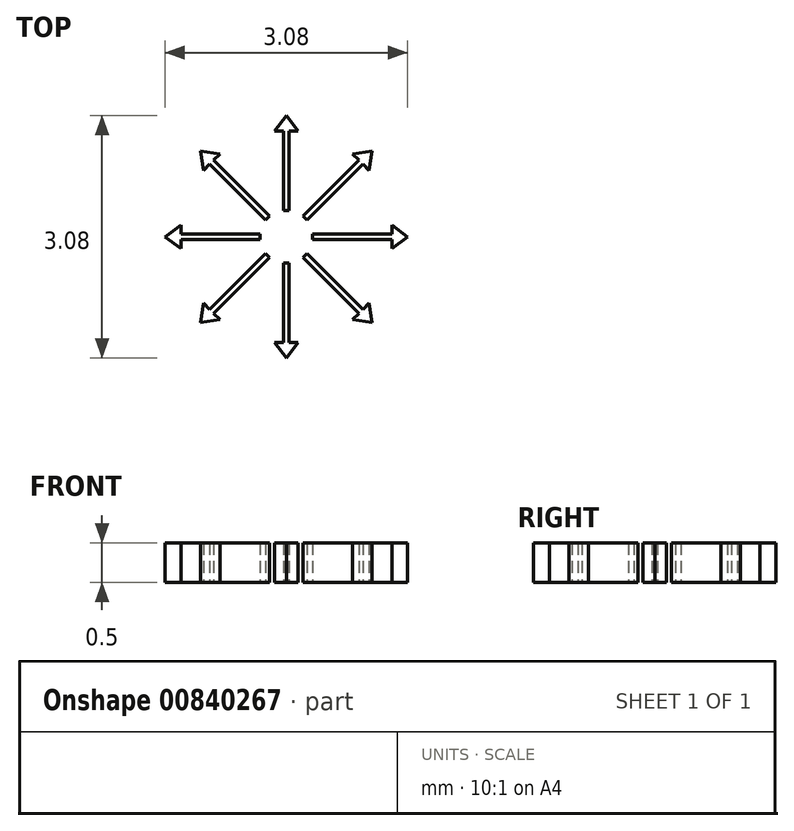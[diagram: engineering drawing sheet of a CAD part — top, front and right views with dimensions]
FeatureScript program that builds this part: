
annotation { "Feature Type Name" : "Feature", "Feature Type Description" : "" }
export const myFeature = defineFeature(function(context is Context, id is Id, definition is map)
    precondition{}
    {
        {
            var Q0;
            Q0=qCreatedBy(makeId("Top.planeOp"),FACE);
            var sketch = newSketch(context, id + "F0", { "sketchPlane" : qUnion([Q0])});
            skPoint(sketch, "E0.center", {"position": v(0, 0) * mm});
            skLineSegment(sketch, "E1", {"start": v(-0.04, 1.34) * mm, "end": v(-0.04, 0.34) * mm});
            skLineSegment(sketch, "E2", {"start": v(0.04, 1.34) * mm, "end": v(0.04, 0.34) * mm});
            skLineSegment(sketch, "E3", {"start": v(-0.04, 0.34) * mm, "end": v(0.04, 0.34) * mm});
            skLineSegment(sketch, "E4", {"start": v(-0.04, 1.34) * mm, "end": v(0.04, 1.34) * mm});
            skLineSegment(sketch, "E5", {"start": v(-0.04, 1.34) * mm, "end": v(-0.15, 1.34) * mm});
            skLineSegment(sketch, "E6", {"start": v(-0.15, 1.34) * mm, "end": v(0, 1.54) * mm});
            skLineSegment(sketch, "E7", {"start": v(0.04, 1.34) * mm, "end": v(0.15, 1.34) * mm});
            skLineSegment(sketch, "E8", {"start": v(0.15, 1.34) * mm, "end": v(0, 1.54) * mm});
            skLineSegment(sketch, "E9.1.0", {"start": v(-0.92, 0.97) * mm, "end": v(-0.21, 0.26) * mm});
            skLineSegment(sketch, "E9.1.1", {"start": v(-1.05, 0.84) * mm, "end": v(-1.09, 1.09) * mm});
            skLineSegment(sketch, "E9.1.2", {"start": v(-0.97, 0.92) * mm, "end": v(-0.26, 0.21) * mm});
            skLineSegment(sketch, "E9.1.4", {"start": v(-0.84, 1.05) * mm, "end": v(-1.09, 1.09) * mm});
            skLineSegment(sketch, "E9.1.5", {"start": v(-0.97, 0.92) * mm, "end": v(-1.05, 0.84) * mm});
            skLineSegment(sketch, "E9.1.6", {"start": v(-0.26, 0.21) * mm, "end": v(-0.21, 0.26) * mm});
            skLineSegment(sketch, "E9.1.7", {"start": v(-0.92, 0.97) * mm, "end": v(-0.84, 1.05) * mm});
            skLineSegment(sketch, "E9.1.8", {"start": v(-0.97, 0.92) * mm, "end": v(-0.92, 0.97) * mm});
            skLineSegment(sketch, "E9.2.0", {"start": v(-1.34, 0.04) * mm, "end": v(-0.34, 0.04) * mm});
            skLineSegment(sketch, "E9.2.1", {"start": v(-1.34, -0.15) * mm, "end": v(-1.54, 0) * mm});
            skLineSegment(sketch, "E9.2.2", {"start": v(-1.34, -0.04) * mm, "end": v(-0.34, -0.04) * mm});
            skLineSegment(sketch, "E9.2.4", {"start": v(-1.34, 0.15) * mm, "end": v(-1.54, 0) * mm});
            skLineSegment(sketch, "E9.2.5", {"start": v(-1.34, -0.04) * mm, "end": v(-1.34, -0.15) * mm});
            skLineSegment(sketch, "E9.2.6", {"start": v(-0.34, -0.04) * mm, "end": v(-0.34, 0.04) * mm});
            skLineSegment(sketch, "E9.2.7", {"start": v(-1.34, 0.04) * mm, "end": v(-1.34, 0.15) * mm});
            skLineSegment(sketch, "E9.2.8", {"start": v(-1.34, -0.04) * mm, "end": v(-1.34, 0.04) * mm});
            skLineSegment(sketch, "E9.3.0", {"start": v(-0.97, -0.92) * mm, "end": v(-0.26, -0.21) * mm});
            skLineSegment(sketch, "E9.3.1", {"start": v(-0.84, -1.05) * mm, "end": v(-1.09, -1.09) * mm});
            skLineSegment(sketch, "E9.3.2", {"start": v(-0.92, -0.97) * mm, "end": v(-0.21, -0.26) * mm});
            skLineSegment(sketch, "E9.3.4", {"start": v(-1.05, -0.84) * mm, "end": v(-1.09, -1.09) * mm});
            skLineSegment(sketch, "E9.3.5", {"start": v(-0.92, -0.97) * mm, "end": v(-0.84, -1.05) * mm});
            skLineSegment(sketch, "E9.3.6", {"start": v(-0.21, -0.26) * mm, "end": v(-0.26, -0.21) * mm});
            skLineSegment(sketch, "E9.3.7", {"start": v(-0.97, -0.92) * mm, "end": v(-1.05, -0.84) * mm});
            skLineSegment(sketch, "E9.3.8", {"start": v(-0.92, -0.97) * mm, "end": v(-0.97, -0.92) * mm});
            skLineSegment(sketch, "E9.4.0", {"start": v(-0.04, -1.34) * mm, "end": v(-0.04, -0.34) * mm});
            skLineSegment(sketch, "E9.4.1", {"start": v(0.15, -1.34) * mm, "end": v(0, -1.54) * mm});
            skLineSegment(sketch, "E9.4.2", {"start": v(0.04, -1.34) * mm, "end": v(0.04, -0.34) * mm});
            skLineSegment(sketch, "E9.4.4", {"start": v(-0.15, -1.34) * mm, "end": v(0, -1.54) * mm});
            skLineSegment(sketch, "E9.4.5", {"start": v(0.04, -1.34) * mm, "end": v(0.15, -1.34) * mm});
            skLineSegment(sketch, "E9.4.6", {"start": v(0.04, -0.34) * mm, "end": v(-0.04, -0.34) * mm});
            skLineSegment(sketch, "E9.4.7", {"start": v(-0.04, -1.34) * mm, "end": v(-0.15, -1.34) * mm});
            skLineSegment(sketch, "E9.4.8", {"start": v(0.04, -1.34) * mm, "end": v(-0.04, -1.34) * mm});
            skLineSegment(sketch, "E9.5.0", {"start": v(0.92, -0.97) * mm, "end": v(0.21, -0.26) * mm});
            skLineSegment(sketch, "E9.5.1", {"start": v(1.05, -0.84) * mm, "end": v(1.09, -1.09) * mm});
            skLineSegment(sketch, "E9.5.2", {"start": v(0.97, -0.92) * mm, "end": v(0.26, -0.21) * mm});
            skLineSegment(sketch, "E9.5.4", {"start": v(0.84, -1.05) * mm, "end": v(1.09, -1.09) * mm});
            skLineSegment(sketch, "E9.5.5", {"start": v(0.97, -0.92) * mm, "end": v(1.05, -0.84) * mm});
            skLineSegment(sketch, "E9.5.6", {"start": v(0.26, -0.21) * mm, "end": v(0.21, -0.26) * mm});
            skLineSegment(sketch, "E9.5.7", {"start": v(0.92, -0.97) * mm, "end": v(0.84, -1.05) * mm});
            skLineSegment(sketch, "E9.5.8", {"start": v(0.97, -0.92) * mm, "end": v(0.92, -0.97) * mm});
            skLineSegment(sketch, "E10.3.6.0", {"start": v(1.34, 0.15) * mm, "end": v(1.54, 0) * mm});
            skLineSegment(sketch, "E10.6.6.0", {"start": v(1.34, 0.04) * mm, "end": v(0.34, 0.04) * mm});
            skLineSegment(sketch, "E10.8.6.0", {"start": v(1.34, -0.04) * mm, "end": v(0.34, -0.04) * mm});
            skLineSegment(sketch, "E10.10.6.0", {"start": v(1.34, -0.15) * mm, "end": v(1.54, 0) * mm});
            skLineSegment(sketch, "E10.13.6.0", {"start": v(1.34, 0.04) * mm, "end": v(1.34, 0.15) * mm});
            skLineSegment(sketch, "E10.16.6.0", {"start": v(0.34, 0.04) * mm, "end": v(0.34, -0.04) * mm});
            skLineSegment(sketch, "E10.19.6.0", {"start": v(1.34, -0.04) * mm, "end": v(1.34, -0.15) * mm});
            skLineSegment(sketch, "E10.22.6.0", {"start": v(1.34, 0.04) * mm, "end": v(1.34, -0.04) * mm});
            skLineSegment(sketch, "E10.3.7.0", {"start": v(0.84, 1.05) * mm, "end": v(1.09, 1.09) * mm});
            skLineSegment(sketch, "E10.6.7.0", {"start": v(0.92, 0.97) * mm, "end": v(0.21, 0.26) * mm});
            skLineSegment(sketch, "E10.8.7.0", {"start": v(0.97, 0.92) * mm, "end": v(0.26, 0.21) * mm});
            skLineSegment(sketch, "E10.10.7.0", {"start": v(1.05, 0.84) * mm, "end": v(1.09, 1.09) * mm});
            skLineSegment(sketch, "E10.13.7.0", {"start": v(0.92, 0.97) * mm, "end": v(0.84, 1.05) * mm});
            skLineSegment(sketch, "E10.16.7.0", {"start": v(0.21, 0.26) * mm, "end": v(0.26, 0.21) * mm});
            skLineSegment(sketch, "E10.19.7.0", {"start": v(0.97, 0.92) * mm, "end": v(1.05, 0.84) * mm});
            skLineSegment(sketch, "E10.22.7.0", {"start": v(0.92, 0.97) * mm, "end": v(0.97, 0.92) * mm});
            skSolve(sketch);
        }
        {
            var Q0;
            Q0=makeQuery(id+"F0.imprint","IMPRINT",FACE,{"disambiguationData":[TD([[makeQuery(id+"F0.imprint","IMPRINT",EDGE,{"derivedFrom":sQuery(id+"F0.wireOp",EDGE,"E9.5.1")}),-1.0]])]});
            var Q1;
            Q1=makeQuery(id+"F0.imprint","IMPRINT",FACE,{"disambiguationData":[TD([[makeQuery(id+"F0.imprint","IMPRINT",EDGE,{"derivedFrom":sQuery(id+"F0.wireOp",EDGE,"E9.1.0")}),-1.0]])]});
            var Q2;
            Q2=makeQuery(id+"F0.imprint","IMPRINT",FACE,{"disambiguationData":[TD([[makeQuery(id+"F0.imprint","IMPRINT",EDGE,{"derivedFrom":sQuery(id+"F0.wireOp",EDGE,"E9.3.1")}),-1.0]])]});
            var Q3;
            Q3=makeQuery(id+"F0.imprint","IMPRINT",FACE,{"disambiguationData":[TD([[makeQuery(id+"F0.imprint","IMPRINT",EDGE,{"derivedFrom":sQuery(id+"F0.wireOp",EDGE,"E9.4.0")}),-1.0]])]});
            var Q4;
            Q4=makeQuery(id+"F0.imprint","IMPRINT",FACE,{"disambiguationData":[TD([[makeQuery(id+"F0.imprint","IMPRINT",EDGE,{"derivedFrom":sQuery(id+"F0.wireOp",EDGE,"E9.2.1")}),-1.0]])]});
            var Q5;
            Q5=makeQuery(id+"F0.imprint","IMPRINT",FACE,{"disambiguationData":[TD([[makeQuery(id+"F0.imprint","IMPRINT",EDGE,{"derivedFrom":sQuery(id+"F0.wireOp",EDGE,"E9.5.0")}),-1.0]])]});
            var Q6;
            Q6=makeQuery(id+"F0.imprint","IMPRINT",FACE,{"disambiguationData":[TD([[makeQuery(id+"F0.imprint","IMPRINT",EDGE,{"derivedFrom":sQuery(id+"F0.wireOp",EDGE,"E9.1.1")}),-1.0]])]});
            var Q7;
            Q7=makeQuery(id+"F0.imprint","IMPRINT",FACE,{"disambiguationData":[TD([[makeQuery(id+"F0.imprint","IMPRINT",EDGE,{"derivedFrom":sQuery(id+"F0.wireOp",EDGE,"E9.4.1")}),-1.0]])]});
            var Q8;
            Q8=makeQuery(id+"F0.imprint","IMPRINT",FACE,{"disambiguationData":[TD([[makeQuery(id+"F0.imprint","IMPRINT",EDGE,{"derivedFrom":sQuery(id+"F0.wireOp",EDGE,"E9.2.0")}),-1.0]])]});
            var Q9;
            Q9=makeQuery(id+"F0.imprint","IMPRINT",FACE,{"disambiguationData":[TD([[makeQuery(id+"F0.imprint","IMPRINT",EDGE,{"derivedFrom":sQuery(id+"F0.wireOp",EDGE,"E1")}),1.0]])]});
            var Q10;
            Q10=makeQuery(id+"F0.imprint","IMPRINT",FACE,{"disambiguationData":[TD([[makeQuery(id+"F0.imprint","IMPRINT",EDGE,{"derivedFrom":sQuery(id+"F0.wireOp",EDGE,"E9.3.0")}),-1.0]])]});
            var Q11;
            Q11=makeQuery(id+"F0.imprint","IMPRINT",FACE,{"disambiguationData":[TD([[makeQuery(id+"F0.imprint","IMPRINT",EDGE,{"derivedFrom":sQuery(id+"F0.wireOp",EDGE,"E4")}),1.0]])]});
            var Q12;
            Q12=makeQuery(id+"F0.imprint","IMPRINT",FACE,{"disambiguationData":[TD([[makeQuery(id+"F0.imprint","IMPRINT",EDGE,{"derivedFrom":sQuery(id+"F0.wireOp",EDGE,"E10.6.7.0")}),1.0]])]});
            var Q13;
            Q13=makeQuery(id+"F0.imprint","IMPRINT",FACE,{"disambiguationData":[TD([[makeQuery(id+"F0.imprint","IMPRINT",EDGE,{"derivedFrom":sQuery(id+"F0.wireOp",EDGE,"E10.3.6.0")}),-1.0]])]});
            var Q14;
            Q14=makeQuery(id+"F0.imprint","IMPRINT",FACE,{"disambiguationData":[TD([[makeQuery(id+"F0.imprint","IMPRINT",EDGE,{"derivedFrom":sQuery(id+"F0.wireOp",EDGE,"E10.3.7.0")}),-1.0]])]});
            var Q15;
            Q15=makeQuery(id+"F0.imprint","IMPRINT",FACE,{"disambiguationData":[TD([[makeQuery(id+"F0.imprint","IMPRINT",EDGE,{"derivedFrom":sQuery(id+"F0.wireOp",EDGE,"E10.6.6.0")}),1.0]])]});
            extrude(context, id + "F1", {"entities" : qUnion([Q0, Q1, Q2, Q3, Q4, Q5, Q6, Q7, Q8, Q9, Q10, Q11, Q12, Q13, Q14, Q15]), "depth" : .5 * mm, "offsetDistance" : 25 * mm});
        }
    });
